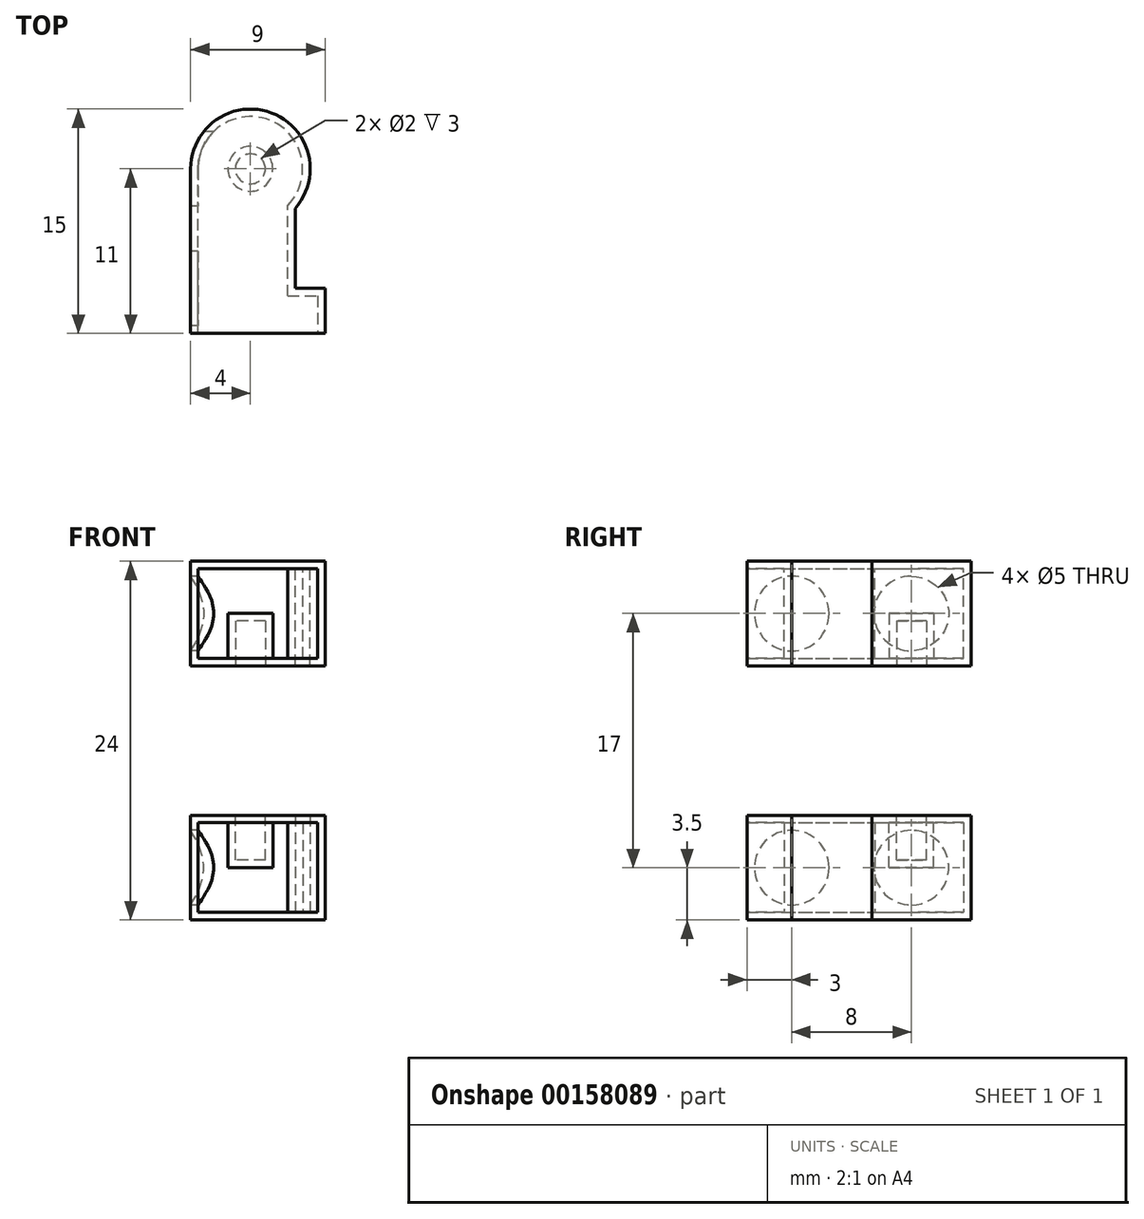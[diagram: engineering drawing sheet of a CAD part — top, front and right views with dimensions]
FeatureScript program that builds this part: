
annotation { "Feature Type Name" : "Feature", "Feature Type Description" : "" }
export const myFeature = defineFeature(function(context is Context, id is Id, definition is map)
    precondition{}
    {
        {
            var Q0;
            Q0=qCreatedBy(makeId("Top.planeOp"),FACE);
            var sketch = newSketch(context, id + "F0", { "sketchPlane" : qUnion([Q0])});
            skLineSegment(sketch, "E0", {"start": v(3, 0) * mm, "end": v(5, 0) * mm});
            skLineSegment(sketch, "E1", {"start": v(5, 0) * mm, "end": v(5, -3) * mm});
            skLineSegment(sketch, "E2", {"start": v(5, -3) * mm, "end": v(-4, -3) * mm});
            skLineSegment(sketch, "E3", {"start": v(-4, -3) * mm, "end": v(-4, 8) * mm});
            skCircle(sketch, "E4", {"center": v(0, 8) * mm, "radius": 4 * mm});
            skLineSegment(sketch, "E5", {"start": v(3, 0) * mm, "end": v(3, 5.35) * mm});
            skSolve(sketch);
        }
        {
            var Q0;
            {var subQ0=sQuery(id+"F0.wireOp",EDGE,"E4");var subQ1=makeQuery(id+"F0.imprint","INTERSECT",VERTEX,{"derivedFrom":[sQuery(id+"F0.wireOp",EDGE,"E3"),subQ0]});Q0=makeQuery(id+"F0.imprint","IMPRINT",FACE,{"disambiguationData":[TD([[makeQuery(id+"F0.imprint","IMPRINT",EDGE,{"disambiguationData":[TD([[subQ1,-1.0]])],"derivedFrom":subQ0}),1.0]])]});}
            var Q1;
            Q1=makeQuery(id+"F0.imprint","IMPRINT",FACE,{"disambiguationData":[TD([[makeQuery(id+"F0.imprint","IMPRINT",EDGE,{"derivedFrom":sQuery(id+"F0.wireOp",EDGE,"E0")}),-1.0]])]});
            extrude(context, id + "F1", {"entities" : qUnion([Q0, Q1]), "depth" : 7 * mm});
        }
        {
            var Q0;
            Q0=makeQuery(id+"F1.opExtrude","CAP_FACE",FACE,{"disambiguationData":[OSD([sQuery(id+"F0.wireOp",EDGE,"E0"),sQuery(id+"F0.wireOp",EDGE,"E1"),sQuery(id+"F0.wireOp",EDGE,"E2"),sQuery(id+"F0.wireOp",EDGE,"E3"),sQuery(id+"F0.wireOp",EDGE,"E4"),sQuery(id+"F0.wireOp",EDGE,"E5")])],"isStart":false});
            var sketch = newSketch(context, id + "F2", { "sketchPlane" : qUnion([Q0])});
            skCircle(sketch, "E6", {"center": v(0, 8) * mm, "radius": 1 * mm});
            skSolve(sketch);
        }
        {
            var Q0;
            Q0=makeQuery(id+"F2.imprint","IMPRINT",FACE,{"disambiguationData":[TD([[makeQuery(id+"F2.imprint","IMPRINT",EDGE,{"derivedFrom":sQuery(id+"F2.wireOp",EDGE,"E6")}),1.0]])]});
            extrude(context, id + "F3", {"entities" : qUnion([Q0]), "operationType" : NewBodyOperationType.REMOVE, "oppositeDirection" : true, "depth" : 3 * mm});
        }
        {
            var Q0;
            Q0=makeQuery(id+"F1.opExtrude","SWEPT_FACE",FACE,{"disambiguationData":[OSD([sQuery(id+"F0.wireOp",EDGE,"E2")])]});
            shell(context, id + "F4", {"entities" : qUnion([Q0]), "thickness" : 0.5 * mm});
        }
        {
            var Q0;
            Q0=makeQuery(id+"F1.opExtrude","SWEPT_FACE",FACE,{"disambiguationData":[OSD([sQuery(id+"F0.wireOp",EDGE,"E3")])]});
            var sketch = newSketch(context, id + "F5", { "sketchPlane" : qUnion([Q0])});
            skCircle(sketch, "E7", {"center": v(0, 3.5) * mm, "radius": 2.5 * mm});
            skCircle(sketch, "E8", {"center": v(-8, 3.5) * mm, "radius": 2.5 * mm});
            skSolve(sketch);
        }
        {
            var Q0;
            {var subQ0=sQuery(id+"F5.wireOp",EDGE,"E8");var subQ1=makeQuery(id+"F1.opExtrude","SWEPT_EDGE",EDGE,{"disambiguationData":[OSD([sQuery(id+"F0.wireOp",EDGE,"E3"),sQuery(id+"F0.wireOp",EDGE,"E4")])]});var subQ2=makeQuery(id+"F5.imprint","INTERSECT",VERTEX,{"disambiguationData":[OD(0.0)],"derivedFrom":[subQ1,subQ0]});Q0=makeQuery(id+"F5.imprint","IMPRINT",FACE,{"disambiguationData":[TD([[makeQuery(id+"F5.imprint","IMPRINT",EDGE,{"disambiguationData":[TD([[subQ2,1.0]])],"derivedFrom":subQ0}),1.0]])]});}
            var Q1;
            {var subQ0=sQuery(id+"F5.wireOp",EDGE,"E8");var subQ1=makeQuery(id+"F1.opExtrude","SWEPT_EDGE",EDGE,{"disambiguationData":[OSD([sQuery(id+"F0.wireOp",EDGE,"E3"),sQuery(id+"F0.wireOp",EDGE,"E4")])]});var subQ2=makeQuery(id+"F5.imprint","INTERSECT",VERTEX,{"disambiguationData":[OD(0.0)],"derivedFrom":[subQ1,subQ0]});Q1=makeQuery(id+"F5.imprint","IMPRINT",FACE,{"disambiguationData":[TD([[makeQuery(id+"F5.imprint","IMPRINT",EDGE,{"disambiguationData":[TD([[subQ2,-1.0]])],"derivedFrom":subQ0}),1.0]])]});}
            var Q2;
            Q2=makeQuery(id+"F5.imprint","IMPRINT",FACE,{"disambiguationData":[TD([[makeQuery(id+"F5.imprint","IMPRINT",EDGE,{"derivedFrom":sQuery(id+"F5.wireOp",EDGE,"E7")}),1.0]])]});
            extrude(context, id + "F6", {"entities" : qUnion([Q0, Q1, Q2]), "operationType" : NewBodyOperationType.REMOVE, "oppositeDirection" : true, "depth" : 2 * mm});
        }
        {
            var Q0;
            Q0=makeQuery(id+"F1.opExtrude","CAP_FACE",FACE,{"disambiguationData":[OSD([sQuery(id+"F0.wireOp",EDGE,"E0"),sQuery(id+"F0.wireOp",EDGE,"E1"),sQuery(id+"F0.wireOp",EDGE,"E2"),sQuery(id+"F0.wireOp",EDGE,"E3"),sQuery(id+"F0.wireOp",EDGE,"E4"),sQuery(id+"F0.wireOp",EDGE,"E5")])],"isStart":false});
            cPlane(context, id + "F7", {"entities" : qUnion([Q0]), "cplaneType" : CPlaneType.OFFSET, "offset" : 5 * mm, "width" : 150 * mm, "height" : 150 * mm});
        }
        {
            var Q0;
            Q0=makeQuery(id+"F1.opExtrude","SWEPT_BODY",BODY,{"disambiguationData":[OSD([sQuery(id+"F0.wireOp",EDGE,"E0"),sQuery(id+"F0.wireOp",EDGE,"E1"),sQuery(id+"F0.wireOp",EDGE,"E2"),sQuery(id+"F0.wireOp",EDGE,"E3"),sQuery(id+"F0.wireOp",EDGE,"E4"),sQuery(id+"F0.wireOp",EDGE,"E5")])]});
            var Q1;
            Q1=qCreatedBy(id+"F7.planeOp",FACE);
            mirror(context, id + "F8", {"entities" : qUnion([Q0]), "mirrorPlane" : qUnion([Q1])});
        }
    });
